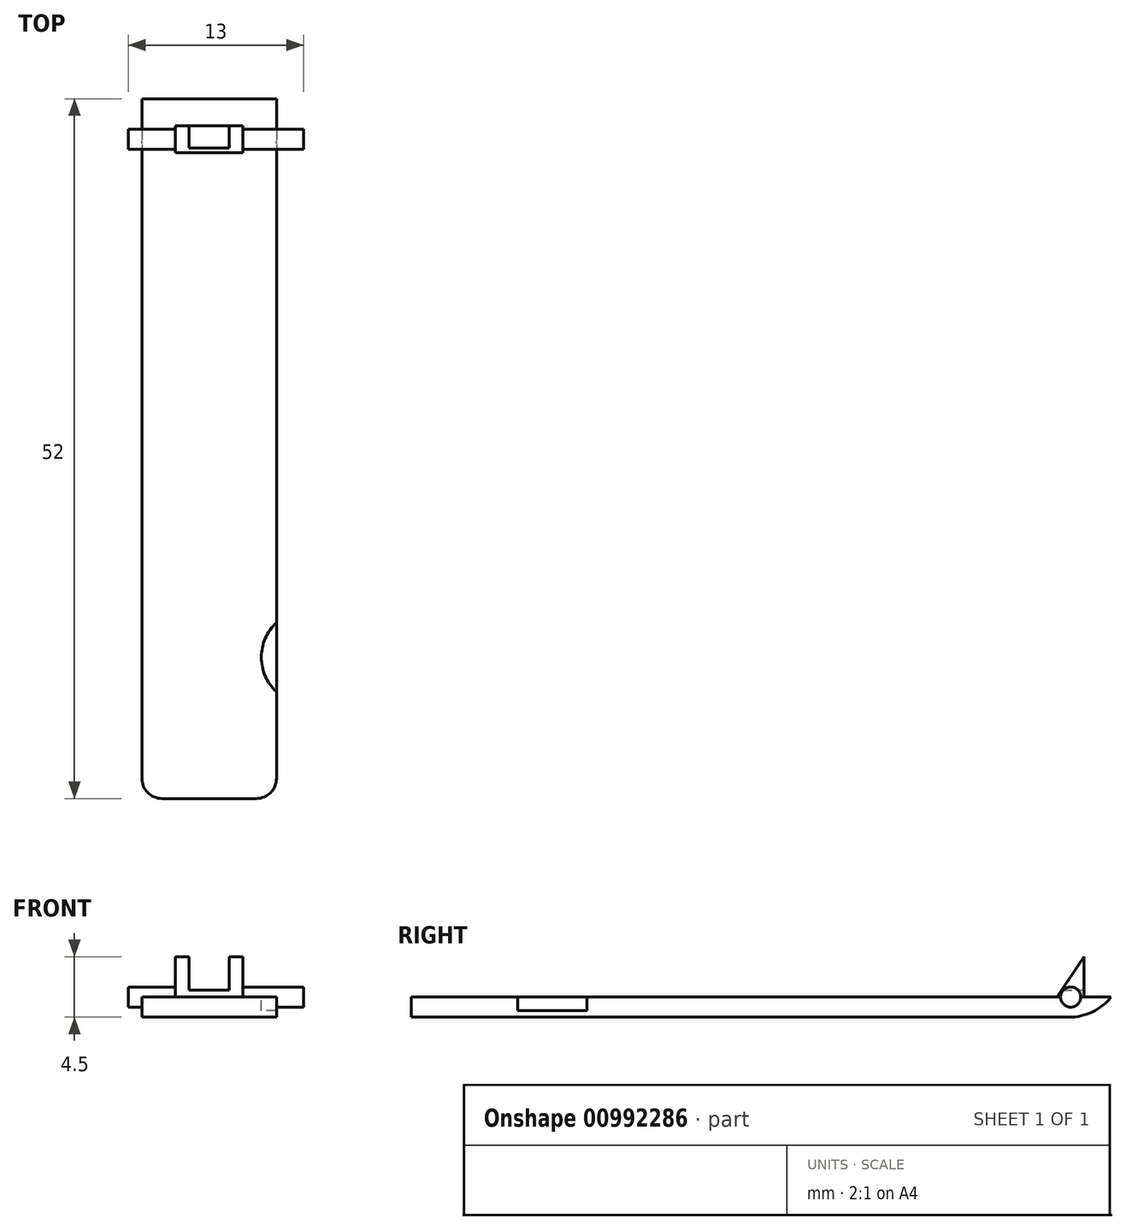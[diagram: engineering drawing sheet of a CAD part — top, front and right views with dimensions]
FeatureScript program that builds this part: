
annotation { "Feature Type Name" : "Feature", "Feature Type Description" : "" }
export const myFeature = defineFeature(function(context is Context, id is Id, definition is map)
    precondition{}
    {
        {
            var Q0;
            Q0=qCreatedBy(makeId("Top.planeOp"),FACE);
            var sketch = newSketch(context, id + "F0", { "sketchPlane" : qUnion([Q0])});
            skLineSegment(sketch, "E0.bottom", {"start": v(0, 0) * mm, "end": v(-10, 0) * mm});
            skLineSegment(sketch, "E0.top", {"start": v(0, 52) * mm, "end": v(-10, 52) * mm});
            skLineSegment(sketch, "E0.left", {"start": v(0, 0) * mm, "end": v(0, 52) * mm});
            skLineSegment(sketch, "E0.right", {"start": v(-10, 0) * mm, "end": v(-10, 52) * mm});
            skSolve(sketch);
        }
        {
            var Q0;
            Q0=makeQuery(id+"F0.imprint","IMPRINT",FACE,{"disambiguationData":[TD([[makeQuery(id+"F0.imprint","IMPRINT",EDGE,{"derivedFrom":sQuery(id+"F0.wireOp",EDGE,"E0.bottom")}),-1.0]])]});
            extrude(context, id + "F1", {"entities" : qUnion([Q0]), "depth" : 1.5 * mm, "offsetDistance" : 25 * mm});
        }
        {
            var Q0;
            Q0=makeQuery(id+"F1.opExtrude","CAP_FACE",FACE,{"disambiguationData":[OSD([sQuery(id+"F0.wireOp",EDGE,"E0.bottom"),sQuery(id+"F0.wireOp",EDGE,"E0.top"),sQuery(id+"F0.wireOp",EDGE,"E0.left"),sQuery(id+"F0.wireOp",EDGE,"E0.right")])],"isStart":false});
            var sketch = newSketch(context, id + "F2", { "sketchPlane" : qUnion([Q0])});
            skLineSegment(sketch, "E1.bottom", {"start": v(-7.5, 50) * mm, "end": v(-2.5, 50) * mm});
            skLineSegment(sketch, "E1.top", {"start": v(-7.5, 48) * mm, "end": v(-2.5, 48) * mm});
            skLineSegment(sketch, "E1.left", {"start": v(-7.5, 50) * mm, "end": v(-7.5, 48) * mm});
            skLineSegment(sketch, "E1.right", {"start": v(-2.5, 50) * mm, "end": v(-2.5, 48) * mm});
            skSolve(sketch);
        }
        {
            var Q0;
            Q0=makeQuery(id+"F2.imprint","IMPRINT",FACE,{"disambiguationData":[TD([[makeQuery(id+"F2.imprint","IMPRINT",EDGE,{"derivedFrom":sQuery(id+"F2.wireOp",EDGE,"E1.bottom")}),-1.0]])]});
            extrude(context, id + "F3", {"entities" : qUnion([Q0]), "operationType" : NewBodyOperationType.ADD, "depth" : 3 * mm, "offsetDistance" : 25 * mm});
        }
        {
            var Q0;
            Q0=makeQuery(id+"F3.opExtrude","SWEPT_FACE",FACE,{"disambiguationData":[OSD([sQuery(id+"F2.wireOp",EDGE,"E1.left")])]});
            var sketch = newSketch(context, id + "F4", { "sketchPlane" : qUnion([Q0])});
            skLineSegment(sketch, "E2", {"start": v(-50, 4.5) * mm, "end": v(-48, 1.5) * mm});
            skLineSegment(sketch, "E3", {"start": v(-48, 1.5) * mm, "end": v(-48, 4.5) * mm});
            skLineSegment(sketch, "E4", {"start": v(-48, 4.5) * mm, "end": v(-50, 4.5) * mm});
            skSolve(sketch);
        }
        {
            var Q0;
            Q0=makeQuery(id+"F4.imprint","IMPRINT",FACE,{"disambiguationData":[TD([[makeQuery(id+"F4.imprint","IMPRINT",EDGE,{"derivedFrom":sQuery(id+"F4.wireOp",EDGE,"E2")}),1.0]])]});
            extrude(context, id + "F5", {"entities" : qUnion([Q0]), "operationType" : NewBodyOperationType.REMOVE, "oppositeDirection" : true, "depth" : 6 * mm, "offsetDistance" : 25 * mm});
        }
        {
            var Q0;
            Q0=makeQuery(id+"F1.opExtrude","SWEPT_FACE",FACE,{"disambiguationData":[OSD([sQuery(id+"F0.wireOp",EDGE,"E0.right")])]});
            var sketch = newSketch(context, id + "F6", { "sketchPlane" : qUnion([Q0])});
            skCircle(sketch, "E5", {"center": v(-49, 1.5) * mm, "radius": 0.75 * mm});
            skSolve(sketch);
        }
        {
            var Q0;
            {var subQ0=sQuery(id+"F6.wireOp",EDGE,"E5");var subQ1=makeQuery(id+"F1.opExtrude","CAP_EDGE",EDGE,{"disambiguationData":[OSD([sQuery(id+"F0.wireOp",EDGE,"E0.right")])],"isStart":false});var subQ2=makeQuery(id+"F6.imprint","INTERSECT",VERTEX,{"disambiguationData":[OD(0.0)],"derivedFrom":[subQ1,subQ0]});Q0=makeQuery(id+"F6.imprint","IMPRINT",FACE,{"disambiguationData":[TD([[makeQuery(id+"F6.imprint","IMPRINT",EDGE,{"disambiguationData":[TD([[subQ2,-1.0]])],"derivedFrom":subQ0}),1.0]])]});}
            var Q1;
            {var subQ0=sQuery(id+"F6.wireOp",EDGE,"E5");var subQ1=makeQuery(id+"F1.opExtrude","CAP_EDGE",EDGE,{"disambiguationData":[OSD([sQuery(id+"F0.wireOp",EDGE,"E0.right")])],"isStart":false});var subQ2=makeQuery(id+"F6.imprint","INTERSECT",VERTEX,{"disambiguationData":[OD(0.0)],"derivedFrom":[subQ1,subQ0]});Q1=makeQuery(id+"F6.imprint","IMPRINT",FACE,{"disambiguationData":[TD([[makeQuery(id+"F6.imprint","IMPRINT",EDGE,{"disambiguationData":[TD([[subQ2,1.0]])],"derivedFrom":subQ0}),1.0]])]});}
            extrude(context, id + "F7", {"entities" : qUnion([Q0, Q1]), "operationType" : NewBodyOperationType.ADD, "depth" : 1 * mm, "offsetDistance" : 25 * mm});
        }
        {
            var Q0;
            {var subQ0=sQuery(id+"F6.wireOp",EDGE,"E5");var subQ1=makeQuery(id+"F1.opExtrude","CAP_EDGE",EDGE,{"disambiguationData":[OSD([sQuery(id+"F0.wireOp",EDGE,"E0.right")])],"isStart":false});var subQ2=makeQuery(id+"F6.imprint","INTERSECT",VERTEX,{"disambiguationData":[OD(0.0)],"derivedFrom":[subQ1,subQ0]});Q0=makeQuery(id+"F6.imprint","IMPRINT",FACE,{"disambiguationData":[TD([[makeQuery(id+"F6.imprint","IMPRINT",EDGE,{"disambiguationData":[TD([[subQ2,-1.0]])],"derivedFrom":subQ0}),1.0]])]});}
            var Q1;
            {var subQ0=sQuery(id+"F6.wireOp",EDGE,"E5");var subQ1=makeQuery(id+"F1.opExtrude","CAP_EDGE",EDGE,{"disambiguationData":[OSD([sQuery(id+"F0.wireOp",EDGE,"E0.right")])],"isStart":false});var subQ2=makeQuery(id+"F6.imprint","INTERSECT",VERTEX,{"disambiguationData":[OD(0.0)],"derivedFrom":[subQ1,subQ0]});Q1=makeQuery(id+"F6.imprint","IMPRINT",FACE,{"disambiguationData":[TD([[makeQuery(id+"F6.imprint","IMPRINT",EDGE,{"disambiguationData":[TD([[subQ2,1.0]])],"derivedFrom":subQ0}),1.0]])]});}
            extrude(context, id + "F8", {"entities" : qUnion([Q0, Q1]), "operationType" : NewBodyOperationType.ADD, "depth" : -12 * mm, "offsetDistance" : 25 * mm});
        }
        {
            var Q0;
            Q0=makeQuery(id+"F1.opExtrude","SWEPT_EDGE",EDGE,{"disambiguationData":[OSD([sQuery(id+"F0.wireOp",EDGE,"E0.bottom"),sQuery(id+"F0.wireOp",EDGE,"E0.right")])]});
            fillet(context, id + "F9", {"entities" : qUnion([Q0]), "radius" : 1.5 * mm, "tangentPropagation" : true, "allowEdgeOverflow" : false});
        }
        {
            var Q0;
            Q0=makeQuery(id+"F1.opExtrude","SWEPT_EDGE",EDGE,{"disambiguationData":[OSD([sQuery(id+"F0.wireOp",EDGE,"E0.bottom"),sQuery(id+"F0.wireOp",EDGE,"E0.left")])]});
            fillet(context, id + "F10", {"entities" : qUnion([Q0]), "radius" : 1.5 * mm, "tangentPropagation" : true, "allowEdgeOverflow" : false});
        }
        {
            var Q0;
            Q0=makeQuery(id+"F2.imprint","IMPRINT",FACE,{"disambiguationData":[TD([[makeQuery(id+"F2.imprint","IMPRINT",EDGE,{"derivedFrom":sQuery(id+"F2.wireOp",EDGE,"E1.bottom")}),1.0]])]});
            var sketch = newSketch(context, id + "F11", { "sketchPlane" : qUnion([Q0])});
            skCircle(sketch, "E6", {"center": v(2.37, 10.5) * mm, "radius": 3.5 * mm});
            skSolve(sketch);
        }
        {
            var Q0;
            {var subQ0=sQuery(id+"F11.wireOp",EDGE,"E6");var subQ1=makeQuery(id+"F2.imprint","IMPRINT",EDGE,{"derivedFrom":makeQuery(id+"F1.opExtrude","CAP_EDGE",EDGE,{"disambiguationData":[OSD([sQuery(id+"F0.wireOp",EDGE,"E0.left")])],"isStart":false})});var subQ2=makeQuery(id+"F11.imprint","INTERSECT",VERTEX,{"disambiguationData":[OD(0.0)],"derivedFrom":[subQ1,subQ0]});Q0=makeQuery(id+"F11.imprint","IMPRINT",FACE,{"disambiguationData":[TD([[makeQuery(id+"F11.imprint","IMPRINT",EDGE,{"disambiguationData":[TD([[subQ2,1.0]])],"derivedFrom":subQ0}),1.0]])]});}
            extrude(context, id + "F12", {"entities" : qUnion([Q0]), "operationType" : NewBodyOperationType.REMOVE, "oppositeDirection" : true, "depth" : 1 * mm, "offsetDistance" : 25 * mm});
        }
        {
            var Q0;
            Q0=makeQuery(id+"F1.opExtrude","CAP_EDGE",EDGE,{"disambiguationData":[OSD([sQuery(id+"F0.wireOp",EDGE,"E0.top")])],"isStart":true});
            fillet(context, id + "F13", {"entities" : qUnion([Q0]), "radius" : 4 * mm, "tangentPropagation" : true, "allowEdgeOverflow" : false});
        }
        {
            var Q0;
            Q0=makeQuery(id+"F3.opExtrude","SWEPT_FACE",FACE,{"disambiguationData":[OSD([sQuery(id+"F2.wireOp",EDGE,"E1.bottom")])]});
            var sketch = newSketch(context, id + "F14", { "sketchPlane" : qUnion([Q0])});
            skLineSegment(sketch, "E7.bottom", {"start": v(3.5, 4.5) * mm, "end": v(6.5, 4.5) * mm});
            skLineSegment(sketch, "E7.top", {"start": v(3.5, 2) * mm, "end": v(6.5, 2) * mm});
            skLineSegment(sketch, "E7.left", {"start": v(3.5, 4.5) * mm, "end": v(3.5, 2) * mm});
            skLineSegment(sketch, "E7.right", {"start": v(6.5, 4.5) * mm, "end": v(6.5, 2) * mm});
            skSolve(sketch);
        }
        {
            var Q0;
            Q0=makeQuery(id+"F14.imprint","IMPRINT",FACE,{"disambiguationData":[TD([[makeQuery(id+"F14.imprint","IMPRINT",EDGE,{"derivedFrom":sQuery(id+"F14.wireOp",EDGE,"E7.bottom")}),1.0]])]});
            extrude(context, id + "F15", {"entities" : qUnion([Q0]), "operationType" : NewBodyOperationType.REMOVE, "oppositeDirection" : true, "depth" : 5 * mm, "offsetDistance" : 25 * mm});
        }
    });
